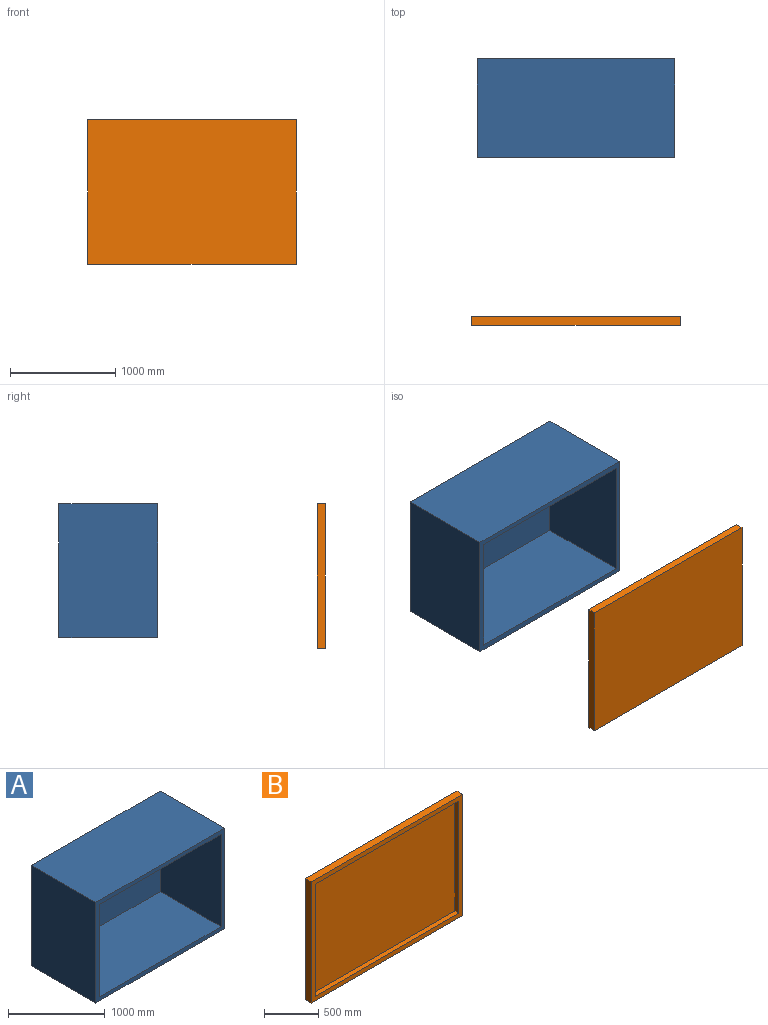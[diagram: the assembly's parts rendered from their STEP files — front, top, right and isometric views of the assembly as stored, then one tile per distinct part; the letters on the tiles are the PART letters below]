
ASSEMBLY  parts=2 mates=2
PART A: 11 faces, bbox 1879.6x939.8x1270 mm
  f0: plane 1879.6x1270mm, normal (0,-1,0), area 309676.8mm2, adj f1,f2,f3,f4,f6,f7,f8,f9
  f1: plane 1879.6x939.8mm, normal (0,0,1), area 1766448.1mm2, adj f0,f2,f4,f5
  f2: plane 1270x939.8mm, normal (-1,0,0), area 1193546mm2, adj f0,f1,f3,f5
  f3: plane 1879.6x939.8mm, normal (0,0,-1), area 1766448.1mm2, adj f0,f2,f4,f5
  f4: plane 1270x939.8mm, normal (1,0,0), area 1193546mm2, adj f0,f1,f3,f5
  f5: plane 1879.6x1270mm, normal (0,1,0), area 2387092mm2, adj f1,f2,f3,f4
  f6: plane 1778x889mm, normal (0,0,-1), area 1580642mm2, adj f0,f7,f9,f10
  f7: plane 1168.4x889mm, normal (1,0,0), area 1038707.6mm2, adj f0,f6,f8,f10
  f8: plane 1778x889mm, normal (0,0,1), area 1580642mm2, adj f0,f7,f9,f10
  f9: plane 1168.4x889mm, normal (-1,0,0), area 1038707.6mm2, adj f0,f6,f8,f10
  f10: plane 1778x1168.4mm, normal (0,-1,0), area 2077415.2mm2, adj f6,f7,f8,f9
PART B: 11 faces, bbox 1981.2x76.2x1371.6 mm
  f0: plane 1981.2x1371.6mm, normal (0,-1,0), area 330321.9mm2, adj f1,f2,f3,f4,f6,f7,f8,f9
  f1: plane 1981.2x76.2mm, normal (0,0,1), area 150967.4mm2, adj f0,f2,f4,f5
  f2: plane 1371.6x76.2mm, normal (-1,0,0), area 104515.9mm2, adj f0,f1,f3,f5
  f3: plane 1981.2x76.2mm, normal (0,0,-1), area 150967.4mm2, adj f0,f2,f4,f5
  f4: plane 1371.6x76.2mm, normal (1,0,0), area 104515.9mm2, adj f0,f1,f3,f5
  f5: plane 1981.2x1371.6mm, normal (0,1,0), area 2717413.9mm2, adj f1,f2,f3,f4
  f6: plane 1879.6x50.8mm, normal (0,0,-1), area 95483.7mm2, adj f0,f7,f9,f10
  f7: plane 1270x50.8mm, normal (1,0,0), area 64516mm2, adj f0,f6,f8,f10
  f8: plane 1879.6x50.8mm, normal (0,0,1), area 95483.7mm2, adj f0,f7,f9,f10
  f9: plane 1270x50.8mm, normal (-1,0,0), area 64516mm2, adj f0,f6,f8,f10
  f10: plane 1879.6x1270mm, normal (0,-1,0), area 2387092mm2, adj f6,f7,f8,f9
PLACE A t=(-1779.9,-947.31,417.51)mm
PLACE B rot(axis=(0,0,1),180deg) t=(-2025.01,-3475.91,619.73)mm
MATE planar A.f2 <-> B.f9  axis (-1,0,0) through (-2656.09,-947.31,724.23)mm
MATE planar B.f6 <-> A.f6  axis (0,0,-1) through (-1716.29,-3425.11,1308.43)mm
